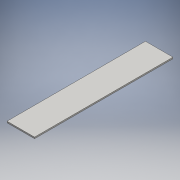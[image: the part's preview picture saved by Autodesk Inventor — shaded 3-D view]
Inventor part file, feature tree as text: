
AUTODESK INVENTOR PART (.ipt)
format: ipt  version: 2016 SP1 (Build 200210100, 210)  size: 103,936 bytes
history: native  units: mm
features: extrude x1, sketch x1
ambient origin geometry x8: Origin, YZ Plane, XZ Plane, XY Plane, X Axis, Y Axis, Z Axis, Center Point
bodies: Solid1 (feature_tree)
feature tree (2):
  extrude  "Extrusion1"  Depth=287.0mm
  sketch  "Sketch1"  dims[d0=57.0mm d1=287.0mm d2=143.5mm d3=28.5mm d4=3.0mm d5=0.0mm]
